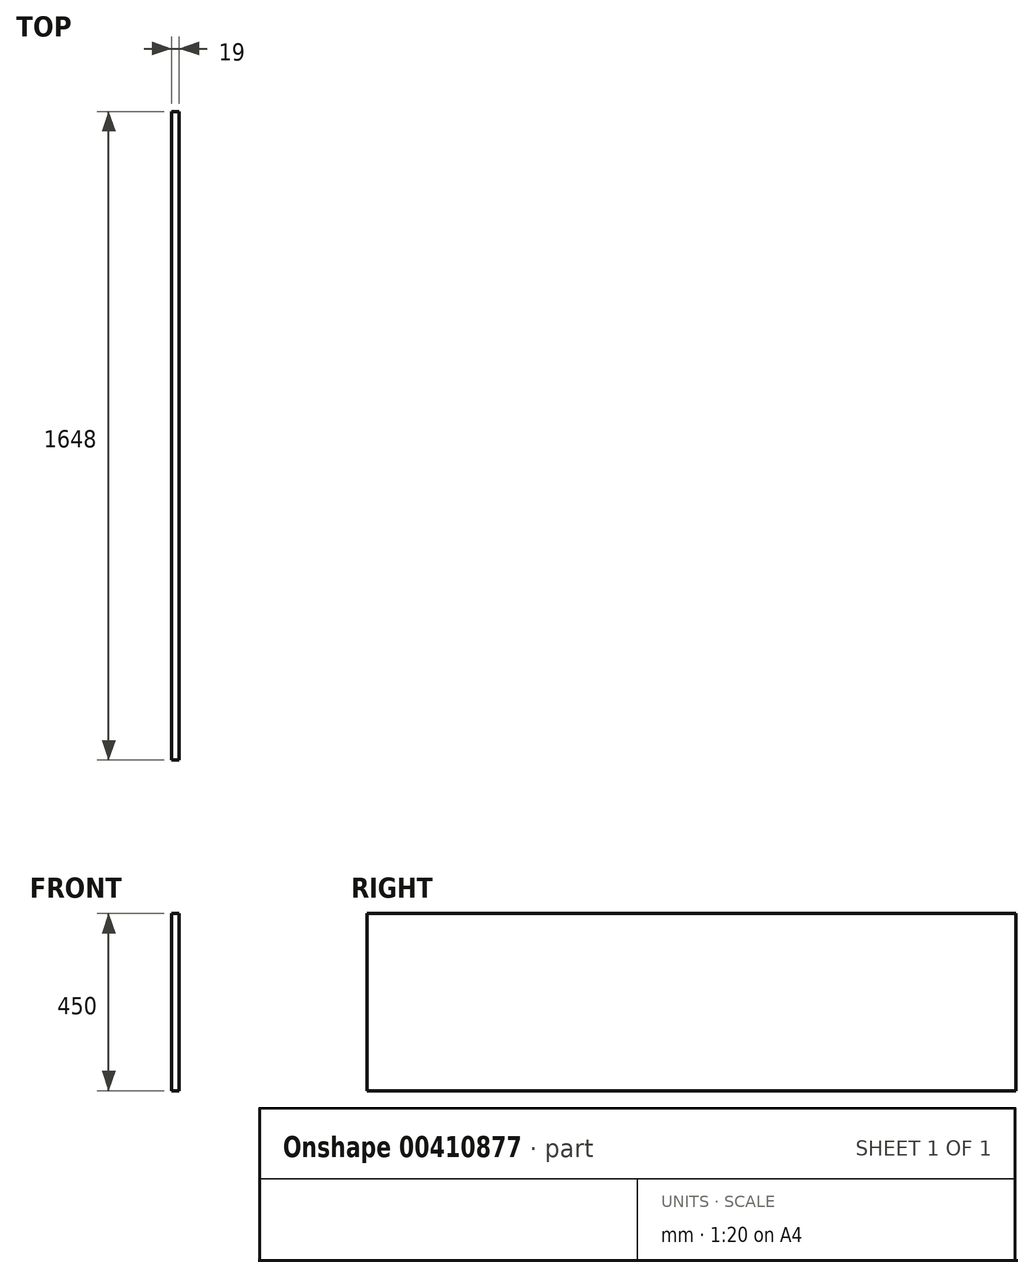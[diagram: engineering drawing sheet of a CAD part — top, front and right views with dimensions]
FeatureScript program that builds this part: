
annotation { "Feature Type Name" : "Feature", "Feature Type Description" : "" }
export const myFeature = defineFeature(function(context is Context, id is Id, definition is map)
    precondition{}
    {
        {
            var Q0;
            Q0=qCreatedBy(makeId("Top.planeOp"),FACE);
            var sketch = newSketch(context, id + "F0", { "sketchPlane" : qUnion([Q0])});
            skLineSegment(sketch, "E0.bottom", {"start": v(61.63, -827.7) * mm, "end": v(80.63, -827.7) * mm});
            skLineSegment(sketch, "E0.top", {"start": v(61.63, 820.3) * mm, "end": v(80.63, 820.3) * mm});
            skLineSegment(sketch, "E0.left", {"start": v(61.63, -827.7) * mm, "end": v(61.63, 820.3) * mm});
            skLineSegment(sketch, "E0.right", {"start": v(80.63, -827.7) * mm, "end": v(80.63, 820.3) * mm});
            skSolve(sketch);
        }
        {
            var Q0;
            Q0=qSketchRegion(id+"F0",true);
            extrude(context, id + "F1", {"entities" : qUnion([Q0]), "depth" : 450 * mm});
        }
    });
